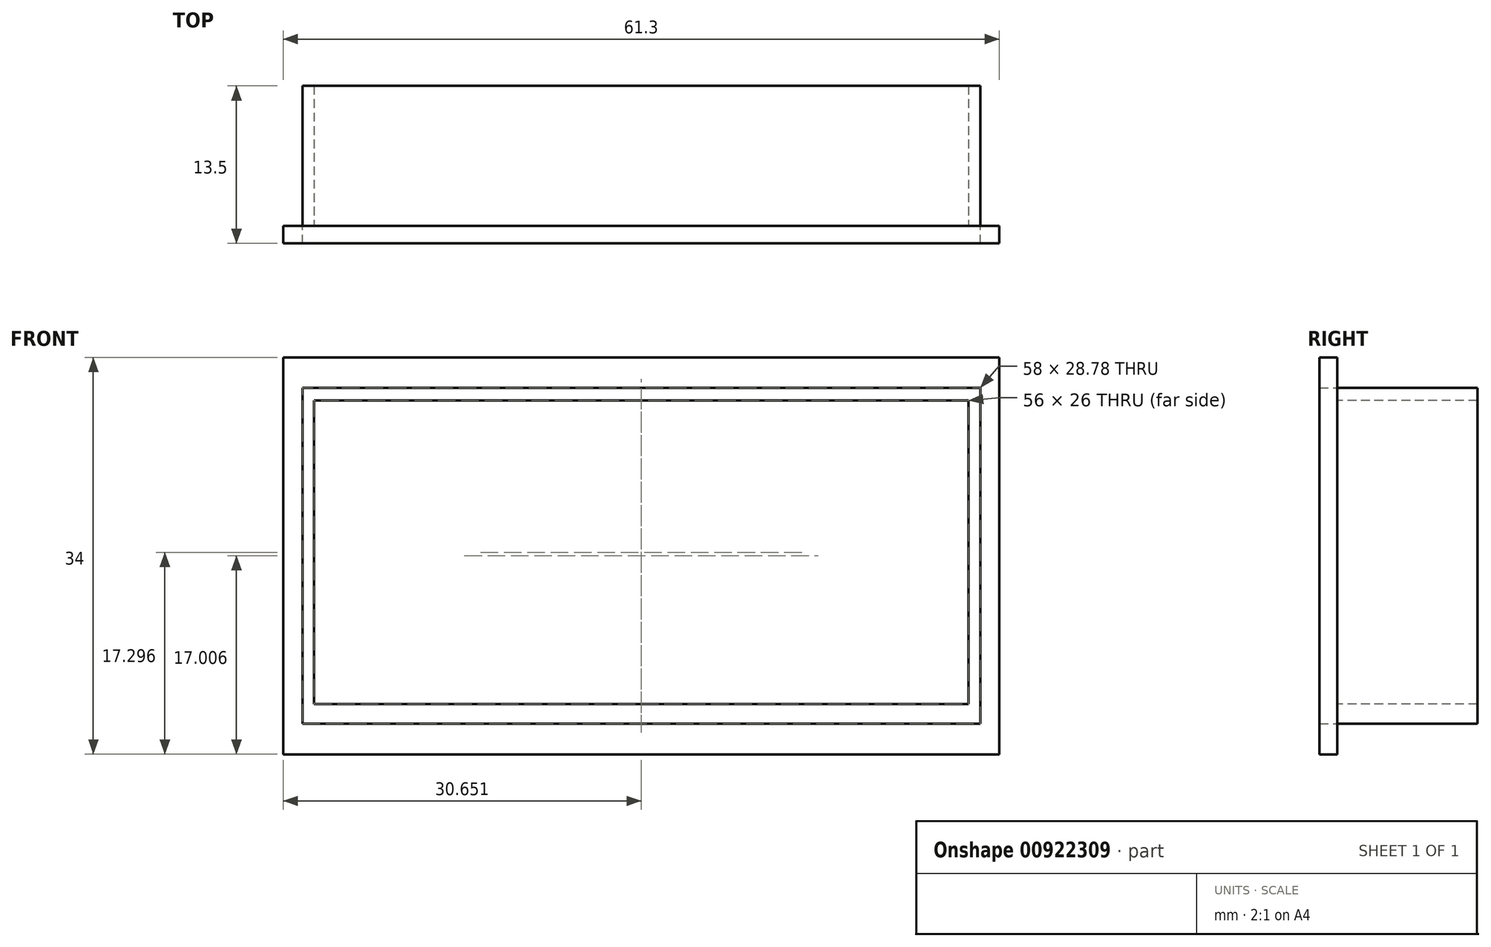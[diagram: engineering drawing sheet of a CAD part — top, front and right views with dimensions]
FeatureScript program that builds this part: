
annotation { "Feature Type Name" : "Feature", "Feature Type Description" : "" }
export const myFeature = defineFeature(function(context is Context, id is Id, definition is map)
    precondition{}
    {
        {
            var Q0;
            Q0=qCreatedBy(makeId("Front.planeOp"),FACE);
            var sketch = newSketch(context, id + "F0", { "sketchPlane" : qUnion([Q0])});
            skLineSegment(sketch, "E0", {"start": v(-200, 0) * mm, "end": v(-200, 200) * mm});
            skLineSegment(sketch, "E1", {"start": v(-200, 200) * mm, "end": v(0, 200) * mm});
            skLineSegment(sketch, "E2", {"start": v(0, 0) * mm, "end": v(0, 50) * mm});
            skLineSegment(sketch, "E3", {"start": v(0, 50) * mm, "end": v(-200, 50) * mm});
            skLineSegment(sketch, "E4", {"start": v(0, 0) * mm, "end": v(-50, 0) * mm});
            skLineSegment(sketch, "E5", {"start": v(-50, 0) * mm, "end": v(-50, 200) * mm});
            skLineSegment(sketch, "E6", {"start": v(0, 200) * mm, "end": v(0, 150) * mm});
            skLineSegment(sketch, "E7", {"start": v(0, 150) * mm, "end": v(-200, 150) * mm});
            skLineSegment(sketch, "E8", {"start": v(-200, 0) * mm, "end": v(-150, 0) * mm});
            skLineSegment(sketch, "E9", {"start": v(-150, 0) * mm, "end": v(-150, 200) * mm});
            skCircle(sketch, "E10", {"center": v(-150, 50) * mm, "radius": 14 * mm});
            skCircle(sketch, "E11", {"center": v(-50, 50) * mm, "radius": 14 * mm});
            skLineSegment(sketch, "E12", {"start": v(-50, 0) * mm, "end": v(-100, 0) * mm});
            skLineSegment(sketch, "E13", {"start": v(-100, 0) * mm, "end": v(-100, 200) * mm});
            skCircle(sketch, "E14", {"center": v(-100, 50) * mm, "radius": 14 * mm});
            skLineSegment(sketch, "E15", {"start": v(-420.33, 76.94) * mm, "end": v(-420.33, 110.94) * mm});
            skLineSegment(sketch, "E16", {"start": v(-420.33, 110.94) * mm, "end": v(-359.03, 110.94) * mm});
            skLineSegment(sketch, "E17", {"start": v(-359.03, 110.94) * mm, "end": v(-359.03, 76.94) * mm});
            skLineSegment(sketch, "E18", {"start": v(-360.68, 79.56) * mm, "end": v(-360.68, 108.34) * mm});
            skLineSegment(sketch, "E19", {"start": v(-360.68, 108.34) * mm, "end": v(-418.68, 108.34) * mm});
            skLineSegment(sketch, "E20", {"start": v(-418.68, 108.34) * mm, "end": v(-418.68, 79.56) * mm});
            skLineSegment(sketch, "E21", {"start": v(-361.68, 81.24) * mm, "end": v(-361.68, 107.24) * mm});
            skLineSegment(sketch, "E22", {"start": v(-361.68, 107.24) * mm, "end": v(-417.68, 107.24) * mm});
            skLineSegment(sketch, "E23", {"start": v(-417.68, 107.24) * mm, "end": v(-417.68, 81.24) * mm});
            skLineSegment(sketch, "E24", {"start": v(-418.68, 79.56) * mm, "end": v(-360.68, 79.56) * mm});
            skLineSegment(sketch, "E25", {"start": v(-420.33, 76.94) * mm, "end": v(-359.03, 76.94) * mm});
            skLineSegment(sketch, "E26", {"start": v(-417.68, 81.24) * mm, "end": v(-361.68, 81.24) * mm});
            skSolve(sketch);
        }
        {
            var Q0;
            Q0=makeQuery(id+"F0.imprint","IMPRINT",FACE,{"disambiguationData":[TD([[makeQuery(id+"F0.imprint","IMPRINT",EDGE,{"derivedFrom":sQuery(id+"F0.wireOp",EDGE,"E18")}),1.0]])]});
            extrude(context, id + "F1", {"entities" : qUnion([Q0]), "oppositeDirection" : true, "depth" : 12 * mm, "offsetDistance" : 25 * mm});
        }
        {
            var Q0;
            Q0=makeQuery(id+"F0.imprint","IMPRINT",FACE,{"disambiguationData":[TD([[makeQuery(id+"F0.imprint","IMPRINT",EDGE,{"derivedFrom":sQuery(id+"F0.wireOp",EDGE,"E15")}),-1.0]])]});
            extrude(context, id + "F2", {"entities" : qUnion([Q0]), "depth" : 1.5 * mm, "offsetDistance" : 25 * mm});
        }
    });
